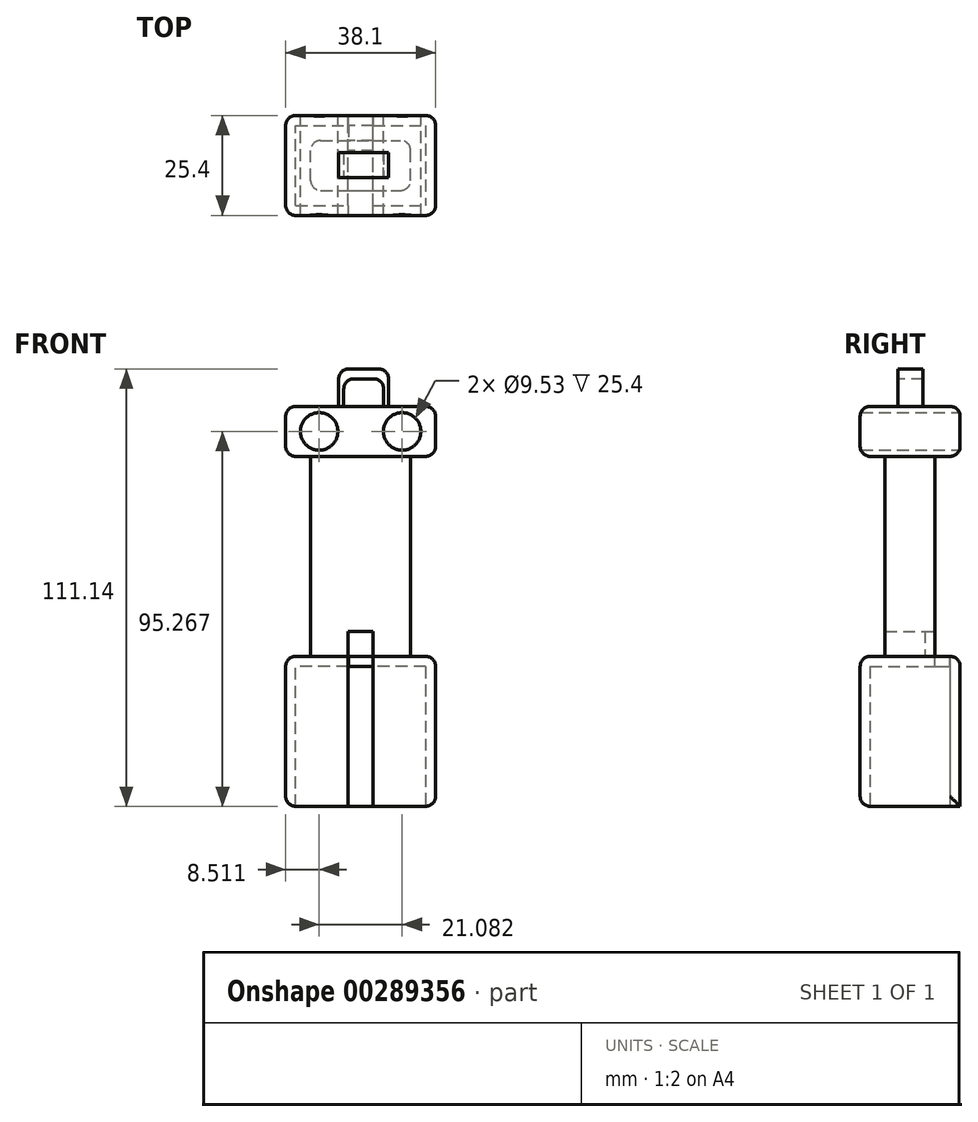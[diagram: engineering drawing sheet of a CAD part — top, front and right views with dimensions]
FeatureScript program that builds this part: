
annotation { "Feature Type Name" : "Feature", "Feature Type Description" : "" }
export const myFeature = defineFeature(function(context is Context, id is Id, definition is map)
    precondition{}
    {
        {
            var Q0;
            Q0=qCreatedBy(makeId("Front.planeOp"),FACE);
            var sketch = newSketch(context, id + "F0", { "sketchPlane" : qUnion([Q0])});
            skLineSegment(sketch, "E0.bottom", {"start": v(-17.78, 53.55) * mm, "end": v(7.62, 53.55) * mm});
            skLineSegment(sketch, "E0.top", {"start": v(-17.78, 2.75) * mm, "end": v(7.62, 2.75) * mm});
            skLineSegment(sketch, "E0.left", {"start": v(-17.78, 53.55) * mm, "end": v(-17.78, 2.75) * mm});
            skLineSegment(sketch, "E0.right", {"start": v(7.62, 53.55) * mm, "end": v(7.62, 2.75) * mm});
            skLineSegment(sketch, "E1.bottom", {"start": v(-24.13, 66.25) * mm, "end": v(13.97, 66.25) * mm});
            skLineSegment(sketch, "E1.top", {"start": v(-24.13, 53.55) * mm, "end": v(13.97, 53.55) * mm});
            skLineSegment(sketch, "E1.left", {"start": v(-24.13, 66.25) * mm, "end": v(-24.13, 53.55) * mm});
            skLineSegment(sketch, "E1.right", {"start": v(13.97, 66.25) * mm, "end": v(13.97, 53.55) * mm});
            skLineSegment(sketch, "E2.bottom", {"start": v(-24.13, 2.73) * mm, "end": v(13.97, 2.73) * mm});
            skLineSegment(sketch, "E2.top", {"start": v(-24.13, -35.37) * mm, "end": v(13.97, -35.37) * mm});
            skLineSegment(sketch, "E2.left", {"start": v(-24.13, 2.73) * mm, "end": v(-24.13, -35.37) * mm});
            skLineSegment(sketch, "E2.right", {"start": v(13.97, 2.73) * mm, "end": v(13.97, -35.37) * mm});
            skLineSegment(sketch, "E3.bottom", {"start": v(-8.25, 9.13) * mm, "end": v(-1.9, 9.13) * mm});
            skLineSegment(sketch, "E3.top", {"start": v(-8.25, -35.32) * mm, "end": v(-1.9, -35.32) * mm});
            skLineSegment(sketch, "E3.left", {"start": v(-8.25, 9.13) * mm, "end": v(-8.25, -35.32) * mm});
            skLineSegment(sketch, "E3.right", {"start": v(-1.9, 9.13) * mm, "end": v(-1.9, -35.32) * mm});
            skPoint(sketch, "E3.middle", {"position": v(-5.08, -13.1) * mm});
            skPoint(sketch, "E3.middle.positionSnap0", {"position": v(-5.08, 2.73) * mm});
            skPoint(sketch, "E3.centerSnap0", {"position": v(-5.08, 2.73) * mm});
            skCircle(sketch, "E4", {"center": v(-15.62, 59.9) * mm, "radius": 4.76 * mm});
            skCircle(sketch, "E5", {"center": v(5.46, 59.9) * mm, "radius": 4.76 * mm});
            skLineSegment(sketch, "E6", {"start": v(-24.13, 53.55) * mm, "end": v(-17.78, 53.55) * mm});
            skLineSegment(sketch, "E7", {"start": v(-24.13, 59.9) * mm, "end": v(13.97, 59.9) * mm, "construction": true});
            skLineSegment(sketch, "E8", {"start": v(-5.08, 66.25) * mm, "end": v(-5.08, 53.55) * mm, "construction": true});
            skLineSegment(sketch, "E9", {"start": v(-17.78, 53.55) * mm, "end": v(-17.78, 66.25) * mm, "construction": true});
            skLineSegment(sketch, "E10", {"start": v(7.62, 53.55) * mm, "end": v(7.62, 66.25) * mm, "construction": true});
            skLineSegment(sketch, "E11", {"start": v(-5.08, 59.9) * mm, "end": v(-15.62, 59.9) * mm, "construction": true});
            skLineSegment(sketch, "E12", {"start": v(-5.08, 59.9) * mm, "end": v(5.46, 59.9) * mm, "construction": true});
            skSolve(sketch);
        }
        {
            var Q0;
            Q0=makeQuery(id+"F0.imprint","IMPRINT",FACE,{"disambiguationData":[TD([[makeQuery(id+"F0.imprint","IMPRINT",EDGE,{"derivedFrom":sQuery(id+"F0.wireOp",EDGE,"E1.bottom")}),-1.0]])]});
            var Q1;
            Q1=makeQuery(id+"F0.imprint","IMPRINT",FACE,{"disambiguationData":[TD([[makeQuery(id+"F0.imprint","IMPRINT",EDGE,{"derivedFrom":sQuery(id+"F0.wireOp",EDGE,"E2.top")}),1.0]])]});
            extrude(context, id + "F1", {"entities" : qUnion([Q0, Q1]), "depth" : 25.4 * mm, "symmetric" : true});
        }
        {
            var Q0;
            {var subQ1=sQuery(id+"F0.wireOp",EDGE,"E0.left");Q0=makeQuery(id+"F0.imprint","IMPRINT",FACE,{"disambiguationData":[TD([[makeQuery(id+"F0.imprint","IMPRINT",EDGE,{"derivedFrom":subQ1}),1.0]])]});}
            extrude(context, id + "F2", {"entities" : qUnion([Q0]), "operationType" : NewBodyOperationType.ADD, "depth" : 12.7 * mm, "symmetric" : true});
        }
        {
            var Q0;
            Q0=makeQuery(id+"F1.opExtrude","CAP_EDGE",EDGE,{"disambiguationData":[OSD([sQuery(id+"F0.wireOp",EDGE,"E1.left")])],"isStart":false});
            var Q1;
            Q1=makeQuery(id+"F1.opExtrude","CAP_EDGE",EDGE,{"disambiguationData":[OSD([sQuery(id+"F0.wireOp",EDGE,"E1.left")])],"isStart":true});
            var Q2;
            Q2=makeQuery(id+"F1.opExtrude","CAP_EDGE",EDGE,{"disambiguationData":[OSD([sQuery(id+"F0.wireOp",EDGE,"E1.right")])],"isStart":false});
            var Q3;
            Q3=makeQuery(id+"F1.opExtrude","CAP_EDGE",EDGE,{"disambiguationData":[OSD([sQuery(id+"F0.wireOp",EDGE,"E1.right")])],"isStart":true});
            var Q4;
            Q4=makeQuery(id+"F1.opExtrude","SWEPT_EDGE",EDGE,{"disambiguationData":[OSD([sQuery(id+"F0.wireOp",EDGE,"E1.bottom"),sQuery(id+"F0.wireOp",EDGE,"E1.right")])]});
            var Q5;
            Q5=makeQuery(id+"F1.opExtrude","CAP_EDGE",EDGE,{"disambiguationData":[OSD([sQuery(id+"F0.wireOp",EDGE,"E1.bottom")])],"isStart":false});
            var Q6;
            Q6=makeQuery(id+"F2.opExtrude","CAP_EDGE",EDGE,{"disambiguationData":[OSD([sQuery(id+"F0.wireOp",EDGE,"E0.right")])],"isStart":false});
            var Q7;
            Q7=makeQuery(id+"F2.opExtrude","CAP_EDGE",EDGE,{"disambiguationData":[OSD([sQuery(id+"F0.wireOp",EDGE,"E0.right")])],"isStart":true});
            var Q8;
            Q8=makeQuery(id+"F2.opExtrude","CAP_EDGE",EDGE,{"disambiguationData":[OSD([sQuery(id+"F0.wireOp",EDGE,"E0.left")])],"isStart":true});
            var Q9;
            Q9=makeQuery(id+"F1.opExtrude","CAP_EDGE",EDGE,{"disambiguationData":[OSD([sQuery(id+"F0.wireOp",EDGE,"E1.bottom")])],"isStart":true});
            var Q10;
            Q10=makeQuery(id+"F1.opExtrude","SWEPT_EDGE",EDGE,{"disambiguationData":[OSD([sQuery(id+"F0.wireOp",EDGE,"E1.bottom"),sQuery(id+"F0.wireOp",EDGE,"E1.left")])]});
            var Q11;
            Q11=makeQuery(id+"F1.opExtrude","CAP_EDGE",EDGE,{"disambiguationData":[OSD([sQuery(id+"F0.wireOp",EDGE,"E2.left")])],"isStart":true});
            var Q12;
            Q12=makeQuery(id+"F1.opExtrude","CAP_EDGE",EDGE,{"disambiguationData":[OSD([sQuery(id+"F0.wireOp",EDGE,"E2.left")])],"isStart":false});
            var Q13;
            {var subQ0=sQuery(id+"F0.wireOp",EDGE,"E2.bottom");Q13=makeQuery(id+"F1.opExtrude","CAP_EDGE",EDGE,{"disambiguationData":[OSD([subQ0]),TDD([makeQuery(id+"F0.imprint","IMPRINT",EDGE,{"disambiguationData":[TD([[makeQuery(id+"F0.imprint","INTERSECT",VERTEX,{"derivedFrom":[subQ0,sQuery(id+"F0.wireOp",EDGE,"E2.left")]}),-1.0]])],"derivedFrom":subQ0})])],"isStart":true});}
            var Q14;
            {var subQ0=sQuery(id+"F0.wireOp",EDGE,"E2.bottom");Q14=makeQuery(id+"F1.opExtrude","CAP_EDGE",EDGE,{"disambiguationData":[OSD([subQ0]),TDD([makeQuery(id+"F0.imprint","IMPRINT",EDGE,{"disambiguationData":[TD([[makeQuery(id+"F0.imprint","INTERSECT",VERTEX,{"derivedFrom":[subQ0,sQuery(id+"F0.wireOp",EDGE,"E2.right")]}),1.0]])],"derivedFrom":subQ0})])],"isStart":true});}
            var Q15;
            Q15=makeQuery(id+"F1.opExtrude","CAP_EDGE",EDGE,{"disambiguationData":[OSD([sQuery(id+"F0.wireOp",EDGE,"E2.right")])],"isStart":true});
            var Q16;
            Q16=makeQuery(id+"F1.opExtrude","SWEPT_EDGE",EDGE,{"disambiguationData":[OSD([sQuery(id+"F0.wireOp",EDGE,"E2.top"),sQuery(id+"F0.wireOp",EDGE,"E2.right")])]});
            var Q17;
            Q17=makeQuery(id+"F1.opExtrude","CAP_EDGE",EDGE,{"disambiguationData":[OSD([sQuery(id+"F0.wireOp",EDGE,"E2.right")])],"isStart":false});
            var Q18;
            Q18=makeQuery(id+"F2.opExtrude","CAP_EDGE",EDGE,{"disambiguationData":[OSD([sQuery(id+"F0.wireOp",EDGE,"E0.left")])],"isStart":false});
            var Q19;
            Q19=makeQuery(id+"F1.opExtrude","CAP_EDGE",EDGE,{"disambiguationData":[OSD([sQuery(id+"F0.wireOp",EDGE,"E2.top")])],"isStart":false});
            var Q20;
            Q20=makeQuery(id+"F1.opExtrude","SWEPT_EDGE",EDGE,{"disambiguationData":[OSD([sQuery(id+"F0.wireOp",EDGE,"E2.top"),sQuery(id+"F0.wireOp",EDGE,"E2.left")])]});
            var Q21;
            Q21=makeQuery(id+"F1.opExtrude","SWEPT_EDGE",EDGE,{"disambiguationData":[OSD([sQuery(id+"F0.wireOp",EDGE,"E2.bottom"),sQuery(id+"F0.wireOp",EDGE,"E2.left")])]});
            var Q22;
            {var subQ0=sQuery(id+"F0.wireOp",EDGE,"E2.bottom");Q22=makeQuery(id+"F1.opExtrude","CAP_EDGE",EDGE,{"disambiguationData":[OSD([subQ0]),TDD([makeQuery(id+"F0.imprint","IMPRINT",EDGE,{"disambiguationData":[TD([[makeQuery(id+"F0.imprint","INTERSECT",VERTEX,{"derivedFrom":[subQ0,sQuery(id+"F0.wireOp",EDGE,"E2.left")]}),-1.0]])],"derivedFrom":subQ0})])],"isStart":false});}
            var Q23;
            {var subQ0=sQuery(id+"F0.wireOp",EDGE,"E2.bottom");Q23=makeQuery(id+"F1.opExtrude","CAP_EDGE",EDGE,{"disambiguationData":[OSD([subQ0]),TDD([makeQuery(id+"F0.imprint","IMPRINT",EDGE,{"disambiguationData":[TD([[makeQuery(id+"F0.imprint","INTERSECT",VERTEX,{"derivedFrom":[subQ0,sQuery(id+"F0.wireOp",EDGE,"E2.right")]}),1.0]])],"derivedFrom":subQ0})])],"isStart":false});}
            var Q24;
            Q24=makeQuery(id+"F1.opExtrude","SWEPT_EDGE",EDGE,{"disambiguationData":[OSD([sQuery(id+"F0.wireOp",EDGE,"E2.bottom"),sQuery(id+"F0.wireOp",EDGE,"E2.right")])]});
            fillet(context, id + "F3", {"entities" : qUnion([Q0, Q1, Q2, Q3, Q4, Q5, Q6, Q7, Q8, Q9, Q10, Q11, Q12, Q13, Q14, Q15, Q16, Q17, Q18, Q19, Q20, Q21, Q22, Q23, Q24]), "radius" : 2.54 * mm, "tangentPropagation" : true, "allowEdgeOverflow" : false});
        }
        {
            var Q0;
            Q0=makeQuery(id+"F1.opExtrude","SWEPT_FACE",FACE,{"disambiguationData":[OSD([sQuery(id+"F0.wireOp",EDGE,"E3.top")])]});
            extrude(context, id + "F4", {"entities" : qUnion([Q0]), "operationType" : NewBodyOperationType.REMOVE, "oppositeDirection" : true, "depth" : 25.4 * mm});
        }
        {
            var Q0;
            Q0=makeQuery(id+"F2.opExtrude","CAP_FACE",FACE,{"disambiguationData":[OSD([sQuery(id+"F0.wireOp",EDGE,"E0.top"),sQuery(id+"F0.wireOp",EDGE,"E0.left"),sQuery(id+"F0.wireOp",EDGE,"E0.right"),sQuery(id+"F0.wireOp",EDGE,"E1.top"),sQuery(id+"F0.wireOp",EDGE,"E3.bottom"),sQuery(id+"F0.wireOp",EDGE,"E3.left"),sQuery(id+"F0.wireOp",EDGE,"E3.right")])],"isStart":true});
            var sketch = newSketch(context, id + "F5", { "sketchPlane" : qUnion([Q0])});
            skLineSegment(sketch, "E13.bottom", {"start": v(1.9, 9.13) * mm, "end": v(8.25, 9.13) * mm});
            skLineSegment(sketch, "E13.top", {"start": v(1.9, 2.75) * mm, "end": v(8.25, 2.75) * mm});
            skLineSegment(sketch, "E13.left", {"start": v(1.9, 9.13) * mm, "end": v(1.9, 2.75) * mm});
            skLineSegment(sketch, "E13.right", {"start": v(8.25, 9.13) * mm, "end": v(8.25, 2.75) * mm});
            skSolve(sketch);
        }
        {
            var Q0;
            Q0=makeQuery(id+"F1.opExtrude","CAP_EDGE",EDGE,{"disambiguationData":[OSD([sQuery(id+"F0.wireOp",EDGE,"E1.top"),sQuery(id+"F0.wireOp",EDGE,"E6")])],"isStart":false});
            fillet(context, id + "F6", {"entities" : qUnion([Q0]), "radius" : 2.54 * mm, "tangentPropagation" : true, "allowEdgeOverflow" : false});
        }
        {
            var Q0;
            Q0 = qSketchRegion(id + "F5", true);
            extrude(context, id + "F7", {"entities" : qUnion([Q0]), "oppositeDirection" : true, "depth" : 2.54 * mm});
        }
        {
            var Q0;
            {var subQ0=sQuery(id+"F0.wireOp",EDGE,"E3.left");Q0=makeQuery(id+"F4.boolean.opBoolean","MERGE",FACE,{"derivedFrom":[makeQuery(id+"F1.opExtrude","SWEPT_FACE",FACE,{"disambiguationData":[OSD([subQ0])]}),makeQuery(id+"F4.opExtrude","SWEPT_FACE",FACE,{"disambiguationData":[OSD([sQuery(id+"F0.wireOp",EDGE,"E3.top"),subQ0])]})]});}
            var sketch = newSketch(context, id + "F8", { "sketchPlane" : qUnion([Q0])});
            skLineSegment(sketch, "E14.bottom", {"start": v(10.16, 2.73) * mm, "end": v(12.7, 2.73) * mm});
            skLineSegment(sketch, "E14.top", {"start": v(10.16, -35.37) * mm, "end": v(12.7, -35.37) * mm});
            skLineSegment(sketch, "E14.left", {"start": v(10.16, 2.73) * mm, "end": v(10.16, -35.37) * mm});
            skLineSegment(sketch, "E14.right", {"start": v(12.7, 2.73) * mm, "end": v(12.7, -35.37) * mm});
            skSolve(sketch);
        }
        {
            var Q0;
            Q0 = qSketchRegion(id + "F8", true);
            var Q1;
            {var subQ0=sQuery(id+"F0.wireOp",EDGE,"E3.right");Q1=makeQuery(id+"F4.boolean.opBoolean","MERGE",FACE,{"derivedFrom":[makeQuery(id+"F1.opExtrude","SWEPT_FACE",FACE,{"disambiguationData":[OSD([subQ0])]}),makeQuery(id+"F4.opExtrude","SWEPT_FACE",FACE,{"disambiguationData":[OSD([sQuery(id+"F0.wireOp",EDGE,"E3.top"),subQ0])]})]});}
            extrude(context, id + "F9", {"entities" : qUnion([Q0]), "endBound" : BoundingType.UP_TO_SURFACE, "endBoundEntityFace" : qUnion([Q1]), "depth" : 25.4 * mm});
        }
        {
            var Q0;
            Q0=makeQuery(id+"F9.opExtrude","SWEPT_EDGE",EDGE,{"disambiguationData":[OSD([sQuery(id+"F8.wireOp",EDGE,"E14.bottom"),sQuery(id+"F8.wireOp",EDGE,"E14.right")])]});
            fillet(context, id + "F10", {"entities" : qUnion([Q0]), "radius" : 2.54 * mm, "tangentPropagation" : true, "allowEdgeOverflow" : false});
        }
        {
            var Q0;
            {var subQ0=sQuery(id+"F0.wireOp",EDGE,"E2.bottom");Q0=makeQuery(id+"F1.opExtrude","SWEPT_FACE",FACE,{"disambiguationData":[OSD([subQ0]),TDD([makeQuery(id+"F0.imprint","IMPRINT",EDGE,{"disambiguationData":[TD([[makeQuery(id+"F0.imprint","INTERSECT",VERTEX,{"derivedFrom":[subQ0,sQuery(id+"F0.wireOp",EDGE,"E2.right")]}),1.0]])],"derivedFrom":subQ0})])]});}
            var sketch = newSketch(context, id + "F11", { "sketchPlane" : qUnion([Q0])});
            skLineSegment(sketch, "E15.bottom", {"start": v(-1.9, 10.16) * mm, "end": v(-8.18, 10.16) * mm});
            skLineSegment(sketch, "E15.top", {"start": v(-1.9, 6.28) * mm, "end": v(-8.18, 6.28) * mm});
            skLineSegment(sketch, "E15.left", {"start": v(-1.9, 10.16) * mm, "end": v(-1.9, 6.28) * mm});
            skLineSegment(sketch, "E15.right", {"start": v(-8.18, 10.16) * mm, "end": v(-8.18, 6.28) * mm});
            skSolve(sketch);
        }
        {
            var Q0;
            Q0 = qSketchRegion(id + "F11", true);
            extrude(context, id + "F12", {"entities" : qUnion([Q0]), "oppositeDirection" : true, "depth" : 2.54 * mm});
        }
        {
            var Q0;
            {var subQ1=sQuery(id+"F0.wireOp",EDGE,"E2.top");var subQ2=sQuery(id+"F0.wireOp",EDGE,"E3.right");Q0=makeQuery(id+"F4.boolean.opBoolean","SPLIT",FACE,{"disambiguationData":[TD([makeQuery(id+"F1.opExtrude","SWEPT_FACE",FACE,{"disambiguationData":[OSD([subQ2])]})])],"derivedFrom":makeQuery(id+"F1.opExtrude","SWEPT_FACE",FACE,{"disambiguationData":[OSD([subQ1])]})});}
            var Q1;
            {var subQ1=sQuery(id+"F0.wireOp",EDGE,"E2.top");var subQ2=sQuery(id+"F0.wireOp",EDGE,"E3.left");Q1=makeQuery(id+"F4.boolean.opBoolean","SPLIT",FACE,{"disambiguationData":[TD([makeQuery(id+"F1.opExtrude","SWEPT_FACE",FACE,{"disambiguationData":[OSD([subQ2])]})])],"derivedFrom":makeQuery(id+"F1.opExtrude","SWEPT_FACE",FACE,{"disambiguationData":[OSD([subQ1])]})});}
            var Q2;
            {var subQ0=sQuery(id+"F0.wireOp",EDGE,"E3.right");Q2=makeQuery(id+"F4.boolean.opBoolean","MERGE",FACE,{"derivedFrom":[makeQuery(id+"F1.opExtrude","SWEPT_FACE",FACE,{"disambiguationData":[OSD([subQ0])]}),makeQuery(id+"F4.opExtrude","SWEPT_FACE",FACE,{"disambiguationData":[OSD([sQuery(id+"F0.wireOp",EDGE,"E3.top"),subQ0])]})]});}
            var Q3;
            {var subQ0=sQuery(id+"F0.wireOp",EDGE,"E3.left");Q3=makeQuery(id+"F4.boolean.opBoolean","MERGE",FACE,{"derivedFrom":[makeQuery(id+"F1.opExtrude","SWEPT_FACE",FACE,{"disambiguationData":[OSD([subQ0])]}),makeQuery(id+"F4.opExtrude","SWEPT_FACE",FACE,{"disambiguationData":[OSD([sQuery(id+"F0.wireOp",EDGE,"E3.top"),subQ0])]})]});}
            shell(context, id + "F13", {"entities" : qUnion([Q0, Q1, Q2, Q3]), "thickness" : 2.54 * mm});
        }
        {
            var Q0;
            Q0=makeQuery(id+"F1.opExtrude","SWEPT_FACE",FACE,{"disambiguationData":[OSD([sQuery(id+"F0.wireOp",EDGE,"E1.bottom")])]});
            var sketch = newSketch(context, id + "F14", { "sketchPlane" : qUnion([Q0])});
            skLineSegment(sketch, "E16.bottom", {"start": v(-10.68, 3.28) * mm, "end": v(2.02, 3.28) * mm});
            skLineSegment(sketch, "E16.top", {"start": v(-10.68, -3.07) * mm, "end": v(2.02, -3.07) * mm});
            skLineSegment(sketch, "E16.left", {"start": v(-10.68, 3.28) * mm, "end": v(-10.68, -3.07) * mm});
            skLineSegment(sketch, "E16.right", {"start": v(2.02, 3.28) * mm, "end": v(2.02, -3.07) * mm});
            skSolve(sketch);
        }
        {
            var Q0;
            Q0 = qSketchRegion(id + "F14", true);
            extrude(context, id + "F15", {"entities" : qUnion([Q0]), "operationType" : NewBodyOperationType.ADD, "depth" : 9.52 * mm});
        }
        {
            var Q0;
            Q0=makeQuery(id+"F15.opExtrude","SWEPT_FACE",FACE,{"disambiguationData":[OSD([sQuery(id+"F14.wireOp",EDGE,"E16.top")])]});
            var sketch = newSketch(context, id + "F16", { "sketchPlane" : qUnion([Q0])});
            skLineSegment(sketch, "E17", {"start": v(-10.68, 69.8) * mm, "end": v(-9.41, 69.8) * mm});
            skPoint(sketch, "E17.startSnap0", {"position": v(-8.78, 69.8) * mm});
            skLineSegment(sketch, "E18", {"start": v(2.02, 69.87) * mm, "end": v(0.75, 69.87) * mm});
            skLineSegment(sketch, "E19", {"start": v(-4.33, 75.77) * mm, "end": v(-4.33, 74.5) * mm});
            skPoint(sketch, "E19.endSnap0", {"position": v(-4.33, 75.77) * mm});
            skLineSegment(sketch, "E20.bottom", {"start": v(0.75, 66.25) * mm, "end": v(-9.37, 66.25) * mm});
            skLineSegment(sketch, "E20.top", {"start": v(0.75, 73.26) * mm, "end": v(-9.37, 73.26) * mm});
            skLineSegment(sketch, "E20.left", {"start": v(0.75, 66.25) * mm, "end": v(0.75, 73.26) * mm});
            skLineSegment(sketch, "E20.right", {"start": v(-9.37, 66.25) * mm, "end": v(-9.37, 73.26) * mm});
            skSolve(sketch);
        }
        {
            var Q0;
            Q0 = qSketchRegion(id + "F16", true);
            extrude(context, id + "F17", {"entities" : qUnion([Q0]), "operationType" : NewBodyOperationType.REMOVE, "endBound" : BoundingType.THROUGH_ALL, "oppositeDirection" : true, "depth" : 25.4 * mm});
        }
        {
            var Q0;
            Q0=makeQuery(id+"F17.boolean.opBoolean","COPY",EDGE,{"derivedFrom":makeQuery(id+"F17.opExtrude","SWEPT_EDGE",EDGE,{"disambiguationData":[OSD([sQuery(id+"F16.wireOp",EDGE,"E20.top"),sQuery(id+"F16.wireOp",EDGE,"E20.right")])]})});
            var Q1;
            Q1=makeQuery(id+"F17.boolean.opBoolean","COPY",EDGE,{"derivedFrom":makeQuery(id+"F17.opExtrude","SWEPT_EDGE",EDGE,{"disambiguationData":[OSD([sQuery(id+"F16.wireOp",EDGE,"E20.top"),sQuery(id+"F16.wireOp",EDGE,"E20.left")])]})});
            fillet(context, id + "F18", {"entities" : qUnion([Q0, Q1]), "radius" : 2.54 * mm, "tangentPropagation" : true, "allowEdgeOverflow" : false});
        }
        {
            var Q0;
            Q0=makeQuery(id+"F15.opExtrude","CAP_EDGE",EDGE,{"disambiguationData":[OSD([sQuery(id+"F14.wireOp",EDGE,"E16.left")])],"isStart":false});
            var Q1;
            Q1=makeQuery(id+"F15.opExtrude","CAP_EDGE",EDGE,{"disambiguationData":[OSD([sQuery(id+"F14.wireOp",EDGE,"E16.right")])],"isStart":false});
            fillet(context, id + "F19", {"entities" : qUnion([Q0, Q1]), "radius" : 2.54 * mm, "tangentPropagation" : true, "allowEdgeOverflow" : false});
        }
    });
